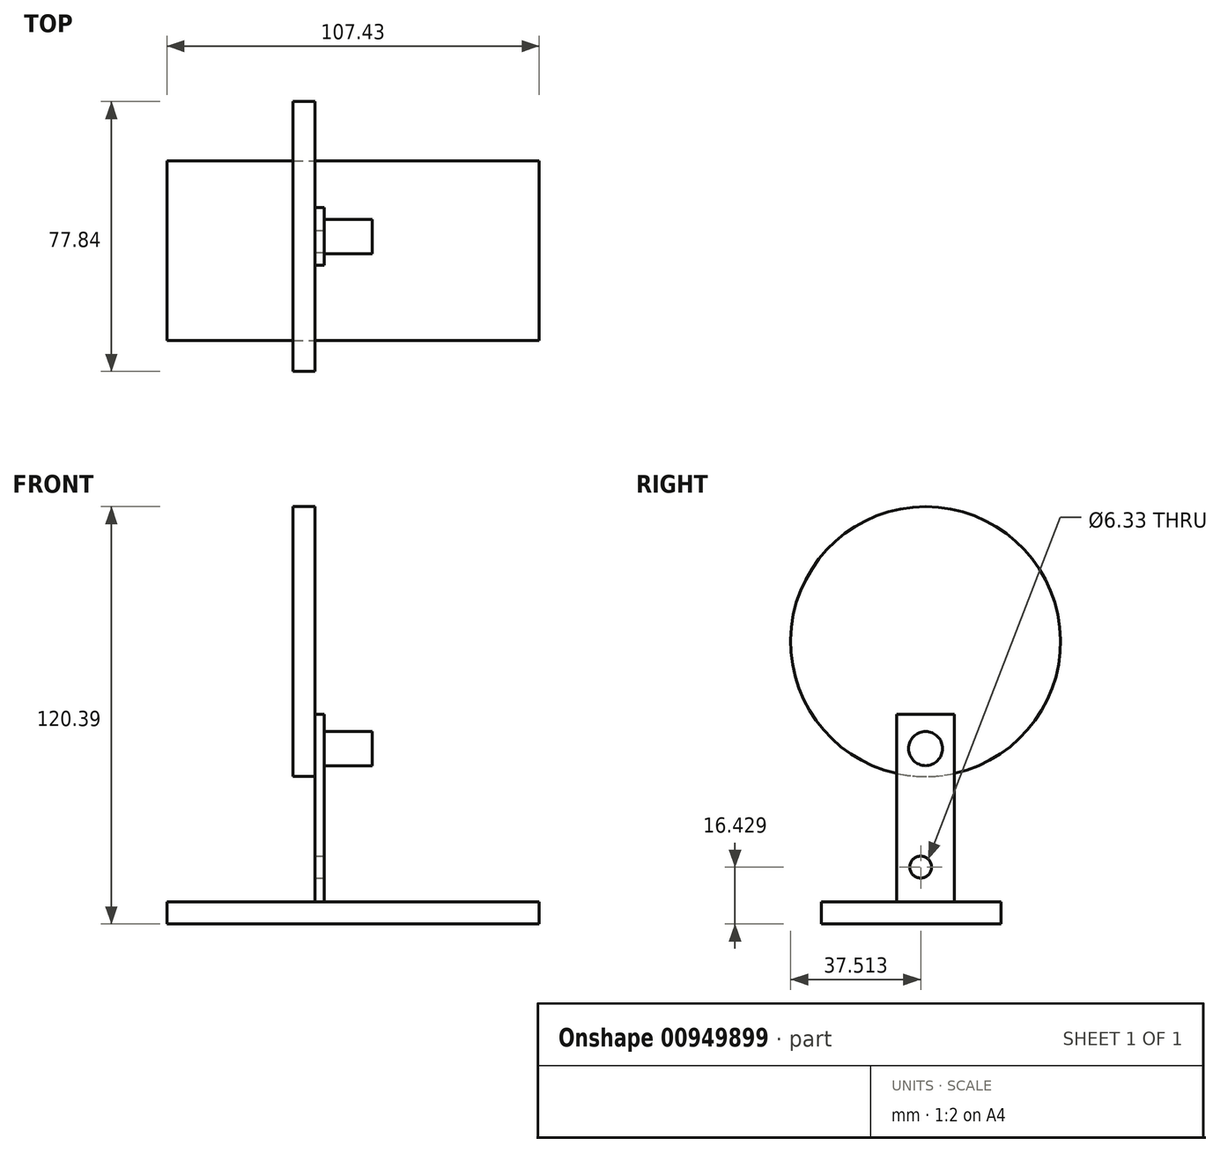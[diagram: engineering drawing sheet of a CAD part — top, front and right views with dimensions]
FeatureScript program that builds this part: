
annotation { "Feature Type Name" : "Feature", "Feature Type Description" : "" }
export const myFeature = defineFeature(function(context is Context, id is Id, definition is map)
    precondition{}
    {
        {
            var Q0;
            Q0=qCreatedBy(makeId("Top.planeOp"),FACE);
            var sketch = newSketch(context, id + "F0", { "sketchPlane" : qUnion([Q0])});
            skLineSegment(sketch, "E0.bottom", {"start": v(-51.73, 30.14) * mm, "end": v(55.7, 30.14) * mm});
            skLineSegment(sketch, "E0.top", {"start": v(-51.73, -21.66) * mm, "end": v(55.7, -21.66) * mm});
            skLineSegment(sketch, "E0.left", {"start": v(-51.73, 30.14) * mm, "end": v(-51.73, -21.66) * mm});
            skLineSegment(sketch, "E0.right", {"start": v(55.7, 30.14) * mm, "end": v(55.7, -21.66) * mm});
            skSolve(sketch);
        }
        {
            var Q0;
            Q0 = qSketchRegion(id + "F0", true);
            extrude(context, id + "F1", {"entities" : qUnion([Q0]), "depth" : 6.35 * mm, "offsetDistance" : 25.4 * mm});
        }
        {
            var Q0;
            Q0=makeQuery(id+"F1.opExtrude","CAP_FACE",FACE,{"disambiguationData":[OSD([sQuery(id+"F0.wireOp",EDGE,"E0.bottom"),sQuery(id+"F0.wireOp",EDGE,"E0.top"),sQuery(id+"F0.wireOp",EDGE,"E0.left"),sQuery(id+"F0.wireOp",EDGE,"E0.right")])],"isStart":false});
            var sketch = newSketch(context, id + "F2", { "sketchPlane" : qUnion([Q0])});
            skLineSegment(sketch, "E1.bottom", {"start": v(-6.28, 0) * mm, "end": v(-9.04, 0) * mm});
            skLineSegment(sketch, "E1.top", {"start": v(-6.28, 16.66) * mm, "end": v(-9.04, 16.66) * mm});
            skLineSegment(sketch, "E1.left", {"start": v(-6.28, 0) * mm, "end": v(-6.28, 16.66) * mm});
            skLineSegment(sketch, "E1.right", {"start": v(-9.04, 0) * mm, "end": v(-9.04, 16.66) * mm});
            skSolve(sketch);
        }
        {
            var Q0;
            Q0 = qSketchRegion(id + "F2", true);
            extrude(context, id + "F3", {"entities" : qUnion([Q0]), "operationType" : NewBodyOperationType.ADD, "depth" : 54.1 * mm, "offsetDistance" : 25.4 * mm});
        }
        {
            var Q0;
            Q0=makeQuery(id+"F3.opExtrude","SWEPT_FACE",FACE,{"disambiguationData":[OSD([sQuery(id+"F2.wireOp",EDGE,"E1.left")])]});
            var sketch = newSketch(context, id + "F4", { "sketchPlane" : qUnion([Q0])});
            skCircle(sketch, "E2", {"center": v(8.33, 50.61) * mm, "radius": 4.9 * mm});
            skPoint(sketch, "E2.centerSnap0", {"position": v(8.33, 60.45) * mm});
            skSolve(sketch);
        }
        {
            var Q0;
            Q0 = qSketchRegion(id + "F4", true);
            extrude(context, id + "F5", {"entities" : qUnion([Q0]), "operationType" : NewBodyOperationType.REMOVE, "endBound" : BoundingType.THROUGH_ALL, "oppositeDirection" : true, "depth" : 25.4 * mm, "offsetDistance" : 25.4 * mm});
        }
        {
            var Q0;
            Q0=makeQuery(id+"F3.opExtrude","SWEPT_FACE",FACE,{"disambiguationData":[OSD([sQuery(id+"F2.wireOp",EDGE,"E1.right")])]});
            var sketch = newSketch(context, id + "F6", { "sketchPlane" : qUnion([Q0])});
            skCircle(sketch, "E3", {"center": v(-8.33, 81.47) * mm, "radius": 38.92 * mm});
            skPoint(sketch, "E3.centerSnap0", {"position": v(-8.33, 60.45) * mm});
            skSolve(sketch);
        }
        {
            var Q0;
            Q0 = qSketchRegion(id + "F6", true);
            extrude(context, id + "F7", {"entities" : qUnion([Q0]), "operationType" : NewBodyOperationType.ADD, "depth" : 6.35 * mm, "offsetDistance" : 25.4 * mm});
        }
        {
            var Q0;
            Q0=makeQuery(id+"F7.boolean.opBoolean","SPLIT",FACE,{"disambiguationData":[TD([makeQuery(id+"F5.boolean.opBoolean","COPY",FACE,{"derivedFrom":makeQuery(id+"F5.opExtrude","SWEPT_FACE",FACE,{"disambiguationData":[OSD([sQuery(id+"F4.wireOp",EDGE,"E2")])]})})])],"derivedFrom":makeQuery(id+"F7.opExtrude","CAP_FACE",FACE,{"disambiguationData":[OSD([sQuery(id+"F6.wireOp",EDGE,"E3")])],"isStart":true})});
            extrude(context, id + "F8", {"entities" : qUnion([Q0]), "operationType" : NewBodyOperationType.ADD, "depth" : 16.5 * mm, "offsetDistance" : 25.4 * mm});
        }
        {
            var Q0;
            Q0=makeQuery(id+"F3.opExtrude","SWEPT_FACE",FACE,{"disambiguationData":[OSD([sQuery(id+"F2.wireOp",EDGE,"E1.left")])]});
            var sketch = newSketch(context, id + "F9", { "sketchPlane" : qUnion([Q0])});
            skCircle(sketch, "E4", {"center": v(6.92, 16.43) * mm, "radius": 3.16 * mm});
            skSolve(sketch);
        }
        {
            var Q0;
            Q0 = qSketchRegion(id + "F9", true);
            extrude(context, id + "F10", {"entities" : qUnion([Q0]), "operationType" : NewBodyOperationType.REMOVE, "endBound" : BoundingType.THROUGH_ALL, "oppositeDirection" : true, "depth" : 25.4 * mm, "offsetDistance" : 25.4 * mm});
        }
    });
